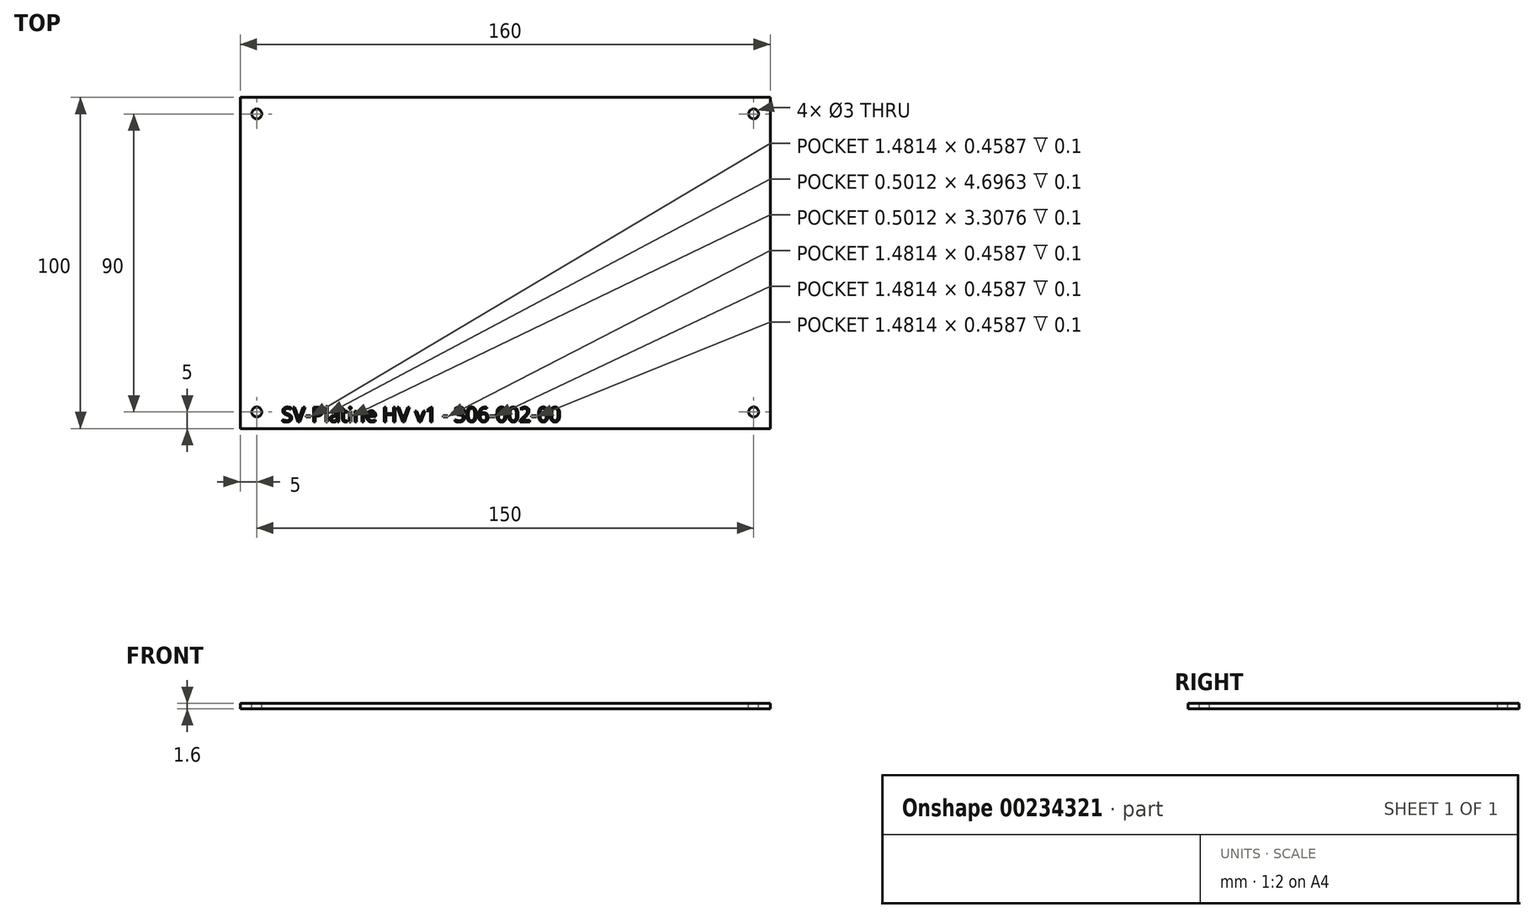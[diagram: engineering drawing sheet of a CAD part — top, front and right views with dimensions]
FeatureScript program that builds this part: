
annotation { "Feature Type Name" : "Feature", "Feature Type Description" : "" }
export const myFeature = defineFeature(function(context is Context, id is Id, definition is map)
    precondition{}
    {
        {
            var Q0;
            Q0=qCreatedBy(makeId("Top.planeOp"),FACE);
            var sketch = newSketch(context, id + "F0", { "sketchPlane" : qUnion([Q0])});
            skLineSegment(sketch, "E0.bottom", {"start": v(80, -50) * mm, "end": v(-80, -50) * mm});
            skLineSegment(sketch, "E0.top", {"start": v(80, 50) * mm, "end": v(-80, 50) * mm});
            skLineSegment(sketch, "E0.left", {"start": v(80, -50) * mm, "end": v(80, 50) * mm});
            skLineSegment(sketch, "E0.right", {"start": v(-80, -50) * mm, "end": v(-80, 50) * mm});
            skCircle(sketch, "E1", {"center": v(-75, -45) * mm, "radius": 1.5 * mm});
            skCircle(sketch, "E2.MirrorC", {"center": v(75, -45) * mm, "radius": 1.5 * mm});
            skCircle(sketch, "E3.MirrorC", {"center": v(-75, 45) * mm, "radius": 1.5 * mm});
            skCircle(sketch, "E4.MirrorC", {"center": v(75, 45) * mm, "radius": 1.5 * mm});
            skSolve(sketch);
        }
        {
            var Q0;
            Q0=makeQuery(id+"F0.imprint","IMPRINT",FACE,{"disambiguationData":[TD([[makeQuery(id+"F0.imprint","IMPRINT",EDGE,{"derivedFrom":sQuery(id+"F0.wireOp",EDGE,"E0.bottom")}),-1.0]])]});
            extrude(context, id + "F1", {"entities" : qUnion([Q0]), "oppositeDirection" : true, "depth" : 1.6 * mm});
        }
        {
            var Q0;
            Q0=makeQuery(id+"F1.opExtrude","CAP_FACE",FACE,{"disambiguationData":[OSD([sQuery(id+"F0.wireOp",EDGE,"E0.bottom"),sQuery(id+"F0.wireOp",EDGE,"E0.top"),sQuery(id+"F0.wireOp",EDGE,"E0.left"),sQuery(id+"F0.wireOp",EDGE,"E0.right"),sQuery(id+"F0.wireOp",EDGE,"E1"),sQuery(id+"F0.wireOp",EDGE,"E2.MirrorC")])],"isStart":true});
            var sketch = newSketch(context, id + "F2", { "sketchPlane" : qUnion([Q0])});
            skText(sketch, "E5", { "text": "SV-Platine HV v1 - 306-002-00", "fontName": "OpenSans-Regular.ttf"});
            const initialGuessF2  = {"E5": [-0.06752, -0.04799, 1, 0, 0.00445]};
            skSetInitialGuess(sketch, initialGuessF2);
            skSolve(sketch);
        }
        {
            var Q0;
            Q0=qSketchRegion(id+"F2",true);
            extrude(context, id + "F3", {"entities" : qUnion([Q0]), "operationType" : NewBodyOperationType.REMOVE, "oppositeDirection" : true, "depth" : .1 * mm});
        }
    });
